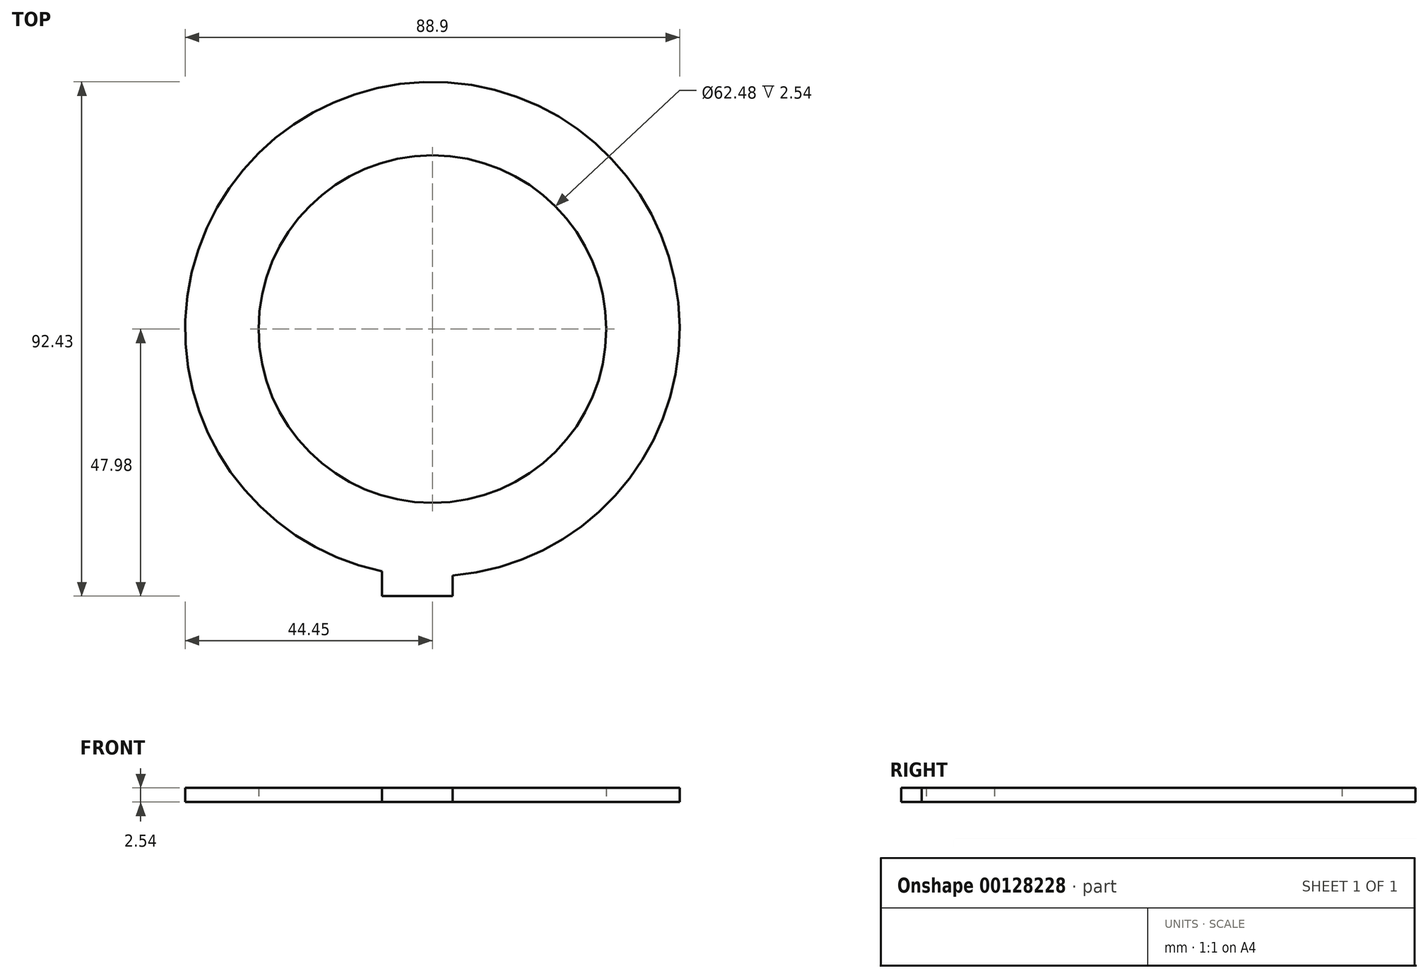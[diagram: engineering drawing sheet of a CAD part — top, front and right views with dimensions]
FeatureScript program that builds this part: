
annotation { "Feature Type Name" : "Feature", "Feature Type Description" : "" }
export const myFeature = defineFeature(function(context is Context, id is Id, definition is map)
    precondition{}
    {
        {
            var Q0;
            Q0=qCreatedBy(makeId("Top.planeOp"),FACE);
            var sketch = newSketch(context, id + "F0", { "sketchPlane" : qUnion([Q0])});
            skCircle(sketch, "E0", {"center": v(0, 0) * mm, "radius": 31.24 * mm});
            skCircle(sketch, "E1", {"center": v(0, 0) * mm, "radius": 44.45 * mm});
            skLineSegment(sketch, "E2.bottom", {"start": v(3.63, -47.98) * mm, "end": v(-9.07, -47.98) * mm});
            skLineSegment(sketch, "E2.left", {"start": v(3.63, -47.98) * mm, "end": v(3.63, -44.3) * mm});
            skLineSegment(sketch, "E2.right", {"start": v(-9.07, -47.98) * mm, "end": v(-9.07, -43.51) * mm});
            skPoint(sketch, "E2.middle", {"position": v(0, -44.45) * mm});
            skPoint(sketch, "E3.trimOffspring.end.orphan", {"position": v(9.07, -40.92) * mm});
            skPoint(sketch, "E4.trimOffspring.end.orphan", {"position": v(-3.63, -40.92) * mm});
            skSolve(sketch);
        }
        {
            var Q0;
            Q0 = qSketchRegion(id + "F0", true);
            extrude(context, id + "F1", {"entities" : qUnion([Q0]), "depth" : 2.54 * mm});
        }
    });
